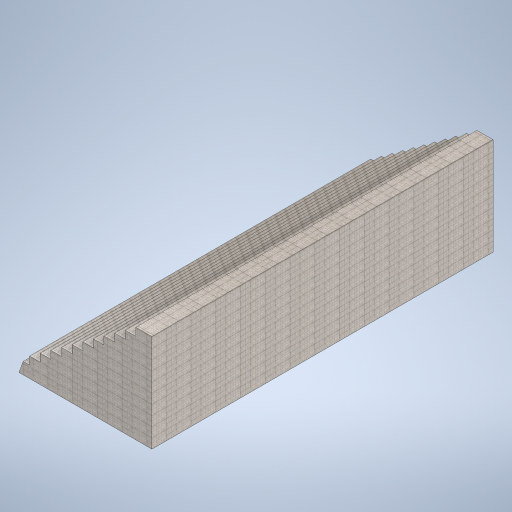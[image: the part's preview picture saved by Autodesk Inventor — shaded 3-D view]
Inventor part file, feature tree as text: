
AUTODESK INVENTOR PART (.ipt)
format: ipt  version: 2024.2 (Build 282272000, 272)  size: 391,680 bytes
history: native  units: in
note: dims shown in document units (in); Inventor stores cm internally (conversion verified against a paired STEP export)
features: other x3, sketch x3
ambient origin geometry x8: Origin, YZ Plane, XZ Plane, XY Plane, X Axis, Y Axis, Z Axis, Center Point
bodies: Solid1 (feature_tree)
feature tree (6):
  other  "front_stair.ipt"
  other  "Solid1::front_stair.ipt"
  other  "TaggingFeature1"
  sketch  "Sketch1"  dims[d0=0.3937in]
  sketch  "Sketch2"
  sketch  "Sketch3"
